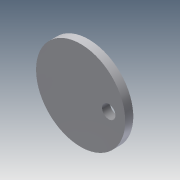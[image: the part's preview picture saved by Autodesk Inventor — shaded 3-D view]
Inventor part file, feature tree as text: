
AUTODESK INVENTOR PART (.ipt)
format: ipt  version: 2013 (Build 170138000, 138)  size: 96,256 bytes
history: native  units: mm
features: sketch x4, extrude x3
ambient origin geometry x8: Origin, YZ Plane, XZ Plane, XY Plane, X Axis, Y Axis, Z Axis, Center Point
bodies: Solid1 (feature_tree)
feature tree (7):
  sketch  "Sketch1"  dims[d0=20.0mm d1=1.8mm d2=0.0mm]
  sketch  "Sketch2"  dims[d3=7.0mm d4=5.0mm]
  extrude  "Extrusion1"  Depth=1.8mm TaperAngle=0.0deg
  extrude  "Extrusion2"  Depth=5.0mm
  extrude  "Extrusion3"  Depth=6.3mm
  sketch  "Sketch3"  dims[d5=2.4mm d6=0.0mm d7=6.3mm]
  sketch  "Sketch4"  dims[d8=3.0mm d9=2.4mm d10=0.0mm]
